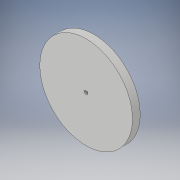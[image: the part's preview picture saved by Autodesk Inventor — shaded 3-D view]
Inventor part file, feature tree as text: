
AUTODESK INVENTOR PART (.ipt)
format: ipt  version: 2018 (Build 220112000, 112)  size: 108,032 bytes
history: native  units: in
note: dims shown in document units (in); Inventor stores cm internally (conversion verified against a paired STEP export)
features: sketch x2, other x2, sheet_metal_op x1
ambient origin geometry x8: Origin, YZ Plane, XZ Plane, XY Plane, X Axis, Y Axis, Z Axis, Center Point
bodies: Solid1 (feature_tree)
feature tree (5):
  sheet_metal_op  "Face1"
  sketch  "Sketch1"  dims[d0=3.0in]
  other  "Plate1"
  sketch  "Sketch2"  dims[d1=0.25in d2=0.117in d4=0.097in d5=0.25in d6=0.0in]
  other  "Cut1"
